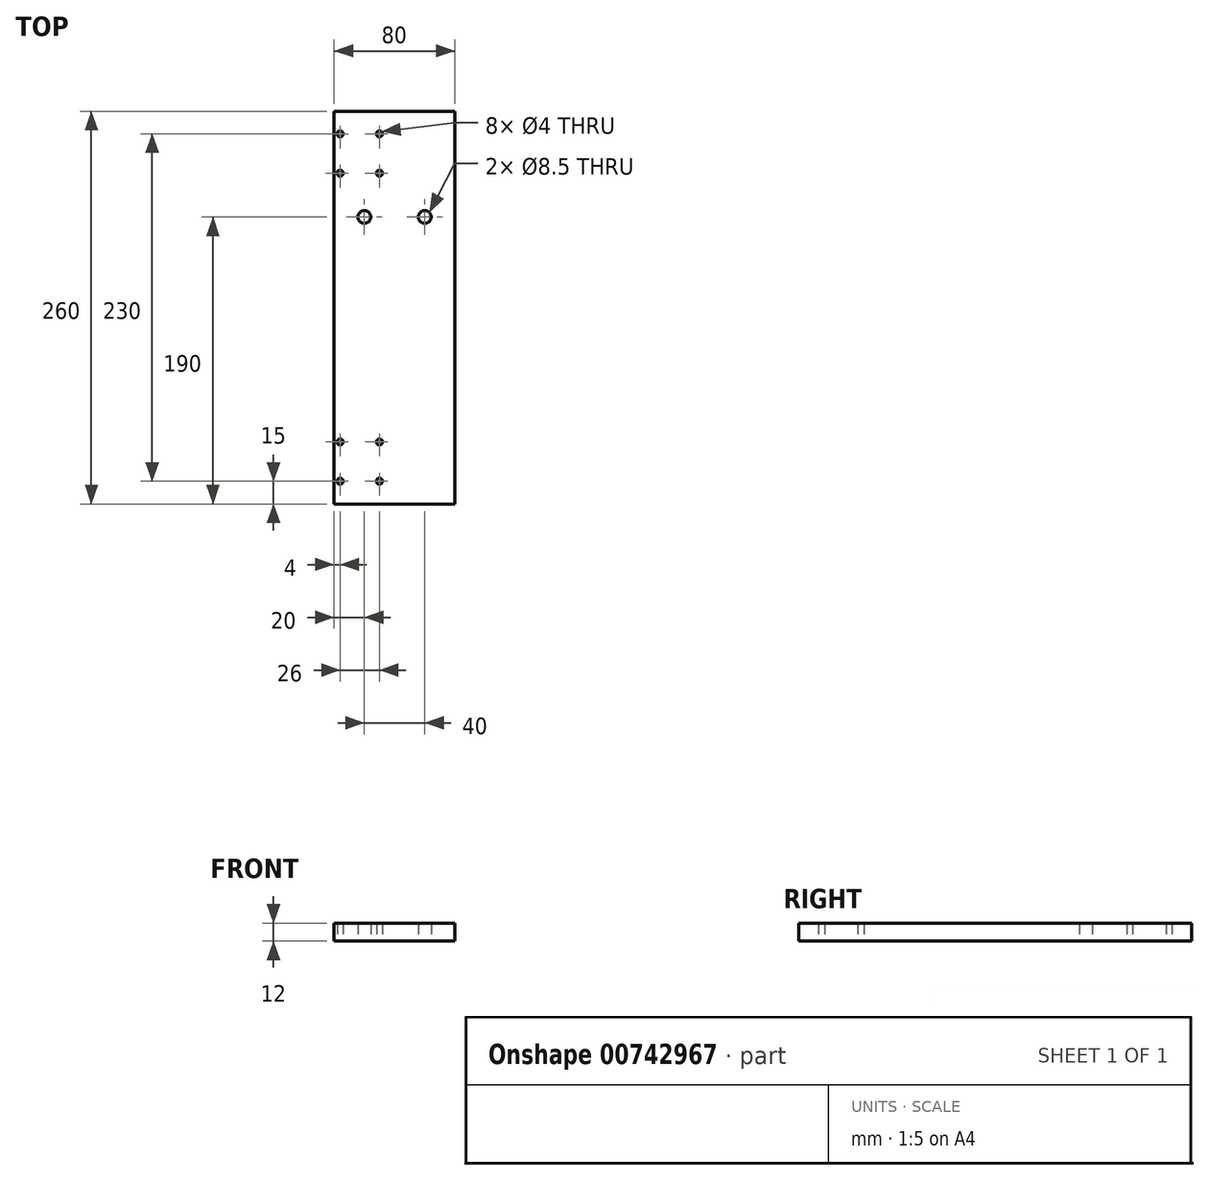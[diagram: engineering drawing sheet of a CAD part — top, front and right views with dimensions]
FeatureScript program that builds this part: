
annotation { "Feature Type Name" : "Feature", "Feature Type Description" : "" }
export const myFeature = defineFeature(function(context is Context, id is Id, definition is map)
    precondition{}
    {
        {
            var Q0;
            Q0=qCreatedBy(makeId("Top.planeOp"),FACE);
            var sketch = newSketch(context, id + "F0", { "sketchPlane" : qUnion([Q0])});
            skLineSegment(sketch, "E0.bottom", {"start": v(40, -130) * mm, "end": v(-40, -130) * mm});
            skLineSegment(sketch, "E0.top", {"start": v(40, 130) * mm, "end": v(-40, 130) * mm});
            skLineSegment(sketch, "E0.left", {"start": v(40, -130) * mm, "end": v(40, 130) * mm});
            skLineSegment(sketch, "E0.right", {"start": v(-40, -130) * mm, "end": v(-40, 130) * mm});
            skPoint(sketch, "E0.middle", {"position": v(0, 0) * mm});
            skCircle(sketch, "E1", {"center": v(-36, 115) * mm, "radius": 2 * mm});
            skLineSegment(sketch, "E2", {"start": v(-23, 115) * mm, "end": v(-23, 89) * mm, "construction": true});
            skCircle(sketch, "E3", {"center": v(-36, 89) * mm, "radius": 2 * mm});
            skCircle(sketch, "E4.MirrorC", {"center": v(-10, 115) * mm, "radius": 2 * mm});
            skCircle(sketch, "E5.MirrorC", {"center": v(-10, 89) * mm, "radius": 2 * mm});
            skCircle(sketch, "E6.MirrorC", {"center": v(-10, -89) * mm, "radius": 2 * mm});
            skCircle(sketch, "E7.MirrorC", {"center": v(-10, -115) * mm, "radius": 2 * mm});
            skCircle(sketch, "E8.MirrorC", {"center": v(-36, -89) * mm, "radius": 2 * mm});
            skLineSegment(sketch, "E9.MirrorCS", {"start": v(-23, -115) * mm, "end": v(-23, -89) * mm, "construction": true});
            skCircle(sketch, "E10.MirrorC", {"center": v(-36, -115) * mm, "radius": 2 * mm});
            skCircle(sketch, "E11", {"center": v(-20, 60) * mm, "radius": 4.25 * mm});
            skCircle(sketch, "E12", {"center": v(20, 60) * mm, "radius": 4.25 * mm});
            skSolve(sketch);
        }
        {
            var Q0;
            Q0 = qSketchRegion(id + "F0", true);
            extrude(context, id + "F1", {"entities" : qUnion([Q0]), "depth" : 12 * mm, "offsetDistance" : 25 * mm});
        }
    });
